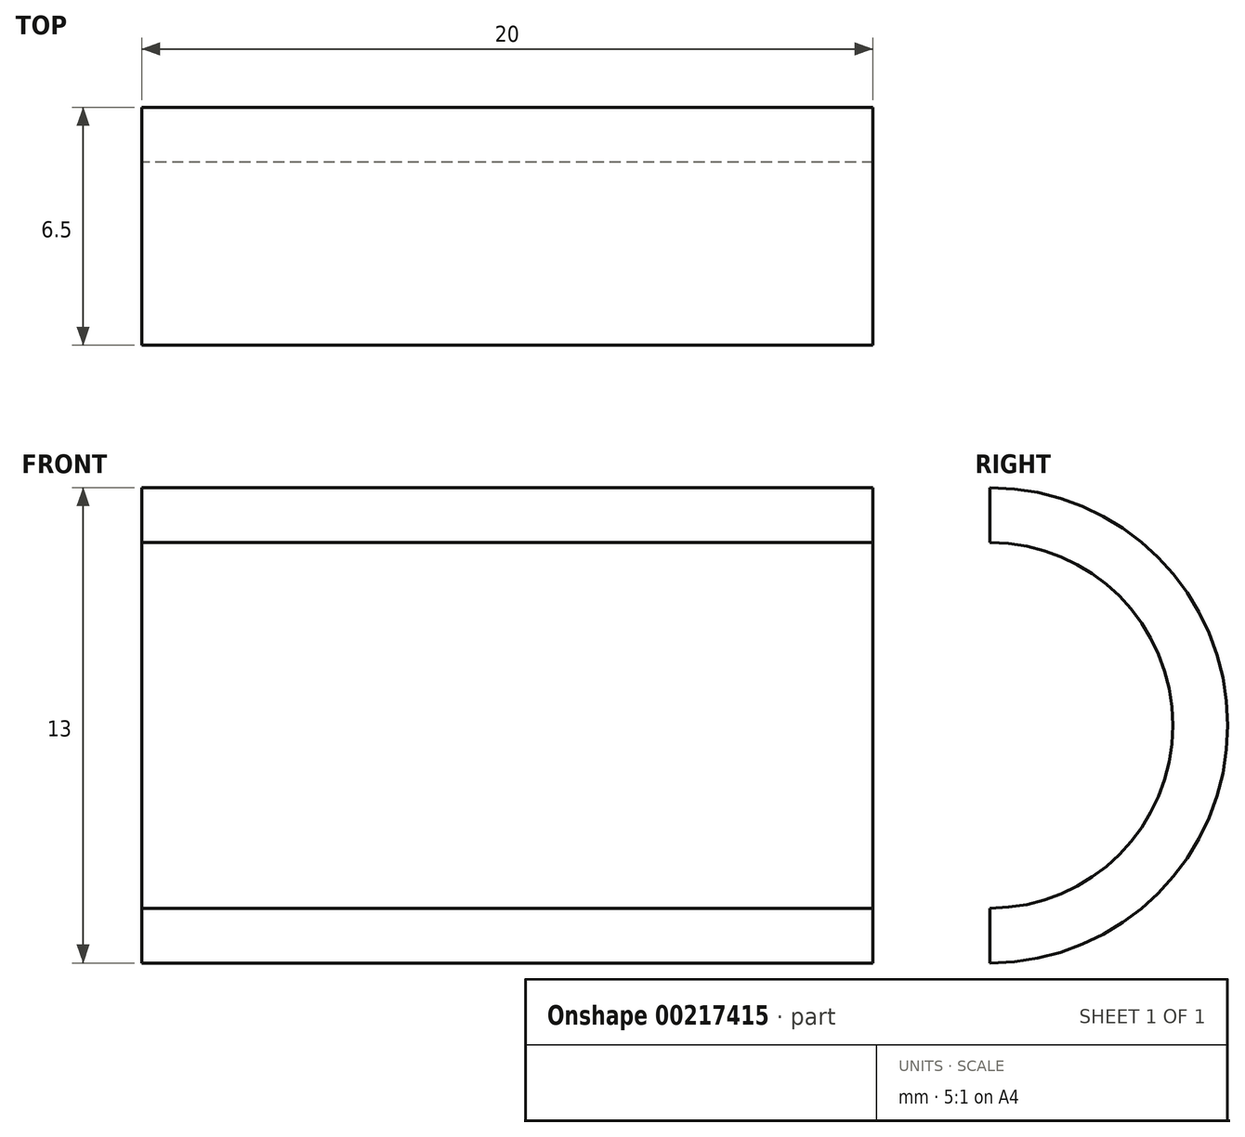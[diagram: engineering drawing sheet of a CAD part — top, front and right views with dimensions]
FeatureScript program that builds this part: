
annotation { "Feature Type Name" : "Feature", "Feature Type Description" : "" }
export const myFeature = defineFeature(function(context is Context, id is Id, definition is map)
    precondition{}
    {
        {
            var Q0;
            Q0=qCreatedBy(makeId("Front.planeOp"),FACE);
            var sketch = newSketch(context, id + "F0", { "sketchPlane" : qUnion([Q0])});
            skLineSegment(sketch, "E0", {"start": v(0, 0) * mm, "end": v(19.48, 0) * mm, "construction": true});
            skLineSegment(sketch, "E1.bottom", {"start": v(0, 6.5) * mm, "end": v(20, 6.5) * mm});
            skLineSegment(sketch, "E1.top", {"start": v(0, 5) * mm, "end": v(20, 5) * mm});
            skLineSegment(sketch, "E1.left", {"start": v(0, 6.5) * mm, "end": v(0, 5) * mm});
            skLineSegment(sketch, "E1.right", {"start": v(20, 6.5) * mm, "end": v(20, 5) * mm});
            skSolve(sketch);
        }
        {
            var Q0;
            Q0 = qSketchRegion(id + "F0", true);
            var Q1;
            Q1=sQuery(id+"F0.wireOp",EDGE,"E0");
            revolve(context, id + "F1", {"entities" : qUnion([Q0]), "axis" : qUnion([Q1]), "revolveType" : RevolveType.FULL});
        }
        {
            var Q0;
            Q0=qCreatedBy(makeId("Top.planeOp"),FACE);
            var sketch = newSketch(context, id + "F2", { "sketchPlane" : qUnion([Q0])});
            skLineSegment(sketch, "E2.bottom", {"start": v(0, 0) * mm, "end": v(22.96, 0) * mm});
            skLineSegment(sketch, "E2.top", {"start": v(0, -8.52) * mm, "end": v(22.96, -8.52) * mm});
            skLineSegment(sketch, "E2.left", {"start": v(0, 0) * mm, "end": v(0, -8.52) * mm});
            skLineSegment(sketch, "E2.right", {"start": v(22.96, 0) * mm, "end": v(22.96, -8.52) * mm});
            skSolve(sketch);
        }
        {
            var Q0;
            Q0 = qSketchRegion(id + "F2", true);
            extrude(context, id + "F3", {"entities" : qUnion([Q0]), "operationType" : NewBodyOperationType.REMOVE, "endBound" : BoundingType.THROUGH_ALL, "oppositeDirection" : true, "depth" : 25.4 * mm, "hasSecondDirection" : true, "secondDirectionBound" : SecondDirectionBoundingType.THROUGH_ALL, "secondDirectionOppositeDirection" : false, "secondDirectionDepth" : 25.4 * mm});
        }
    });
